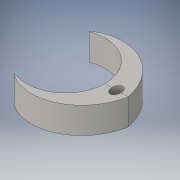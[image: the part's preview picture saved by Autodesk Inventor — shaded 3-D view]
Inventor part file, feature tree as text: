
AUTODESK INVENTOR PART (.ipt)
format: ipt  version: 2016 SP1 (Build 200210100, 210)  size: 163,840 bytes
history: native  units: in
note: dims shown in document units (in); Inventor stores cm internally (conversion verified against a paired STEP export)
features: sketch x4, plane x2, loft x1, extrude x1, mirror x1
ambient origin geometry x8: Origin, YZ Plane, XZ Plane, XY Plane, X Axis, Y Axis, Z Axis, Center Point
bodies: Solid2 (feature_tree)
feature tree (9):
  sketch  "Sketch1"  dims[d0=0.875in d2=1.0in]
  sketch  "Sketch2"  dims[d3=3.0in d21=0.7559in]
  plane  "Work Plane3"
  plane  "Work Plane4"
  loft  "Loft2"
  extrude  "Extrusion2"  Depth=0.7559in
  mirror  "Mirror2"
  sketch  "Sketch7"  dims[d22=90.0deg]
  sketch  "Sketch8"  dims[d24=0.025in d25=1.0in d26=0.0in d27=90.0deg d28=0.0in d29=90.0deg d30=0.0in d31=90.0deg d32=1.9375in d34=0.25in d35=0.175in d36=1.0in d37=1.0in d38=0.0in d39=1.5in d40=1.5in]
